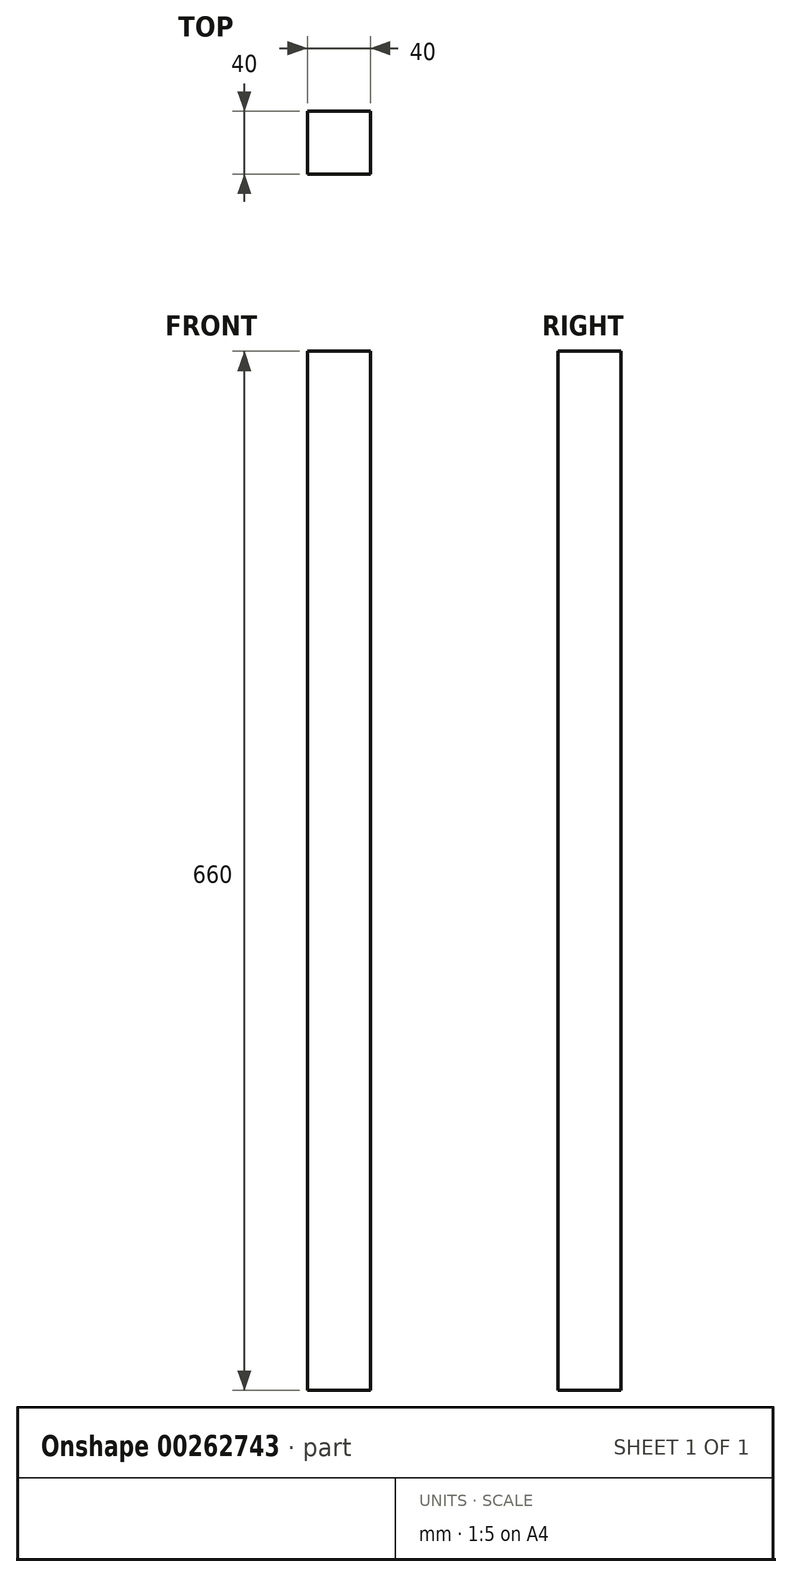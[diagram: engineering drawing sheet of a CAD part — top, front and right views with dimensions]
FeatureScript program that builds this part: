
annotation { "Feature Type Name" : "Feature", "Feature Type Description" : "" }
export const myFeature = defineFeature(function(context is Context, id is Id, definition is map)
    precondition{}
    {
        {
            var Q0;
            Q0=qCreatedBy(makeId("Top.planeOp"),FACE);
            var sketch = newSketch(context, id + "F0", { "sketchPlane" : qUnion([Q0])});
            skLineSegment(sketch, "E0.bottom", {"start": v(0, 0) * mm, "end": v(40, 0) * mm});
            skLineSegment(sketch, "E0.top", {"start": v(0, 40) * mm, "end": v(40, 40) * mm});
            skLineSegment(sketch, "E0.left", {"start": v(0, 0) * mm, "end": v(0, 40) * mm});
            skLineSegment(sketch, "E0.right", {"start": v(40, 0) * mm, "end": v(40, 40) * mm});
            skSolve(sketch);
        }
        {
            var Q0;
            Q0 = qSketchRegion(id + "F0", true);
            extrude(context, id + "F1", {"entities" : qUnion([Q0]), "depth" : 660 * mm});
        }
    });
